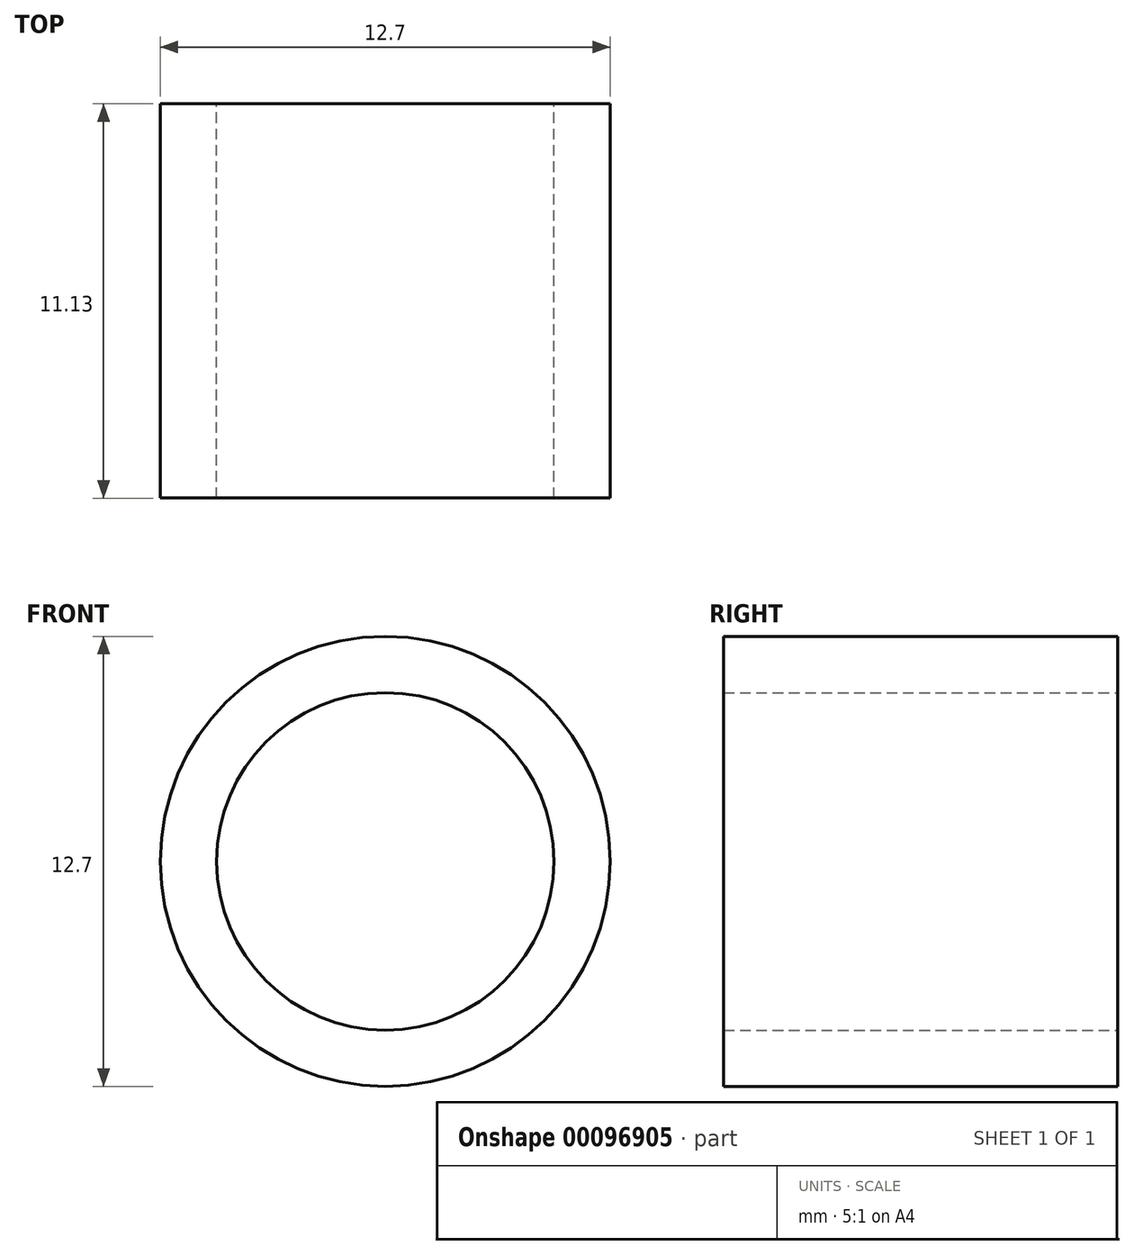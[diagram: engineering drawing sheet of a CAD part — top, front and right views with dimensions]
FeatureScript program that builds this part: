
annotation { "Feature Type Name" : "Feature", "Feature Type Description" : "" }
export const myFeature = defineFeature(function(context is Context, id is Id, definition is map)
    precondition{}
    {
        {
            var Q0;
            Q0=qCreatedBy(makeId("Front.planeOp"),FACE);
            var sketch = newSketch(context, id + "F0", { "sketchPlane" : qUnion([Q0])});
            skCircle(sketch, "E0", {"center": v(0, 0) * mm, "radius": 6.35 * mm});
            skCircle(sketch, "E1", {"center": v(0, 0) * mm, "radius": 4.76 * mm});
            skSolve(sketch);
        }
        {
            var Q0;
            Q0=makeQuery(id+"F0.imprint","IMPRINT",FACE,{"disambiguationData":[TD([[makeQuery(id+"F0.imprint","IMPRINT",EDGE,{"derivedFrom":sQuery(id+"F0.wireOp",EDGE,"E0")}),1.0]])]});
            extrude(context, id + "F1", {"entities" : qUnion([Q0]), "depth" : 11.13 * mm});
        }
    });
